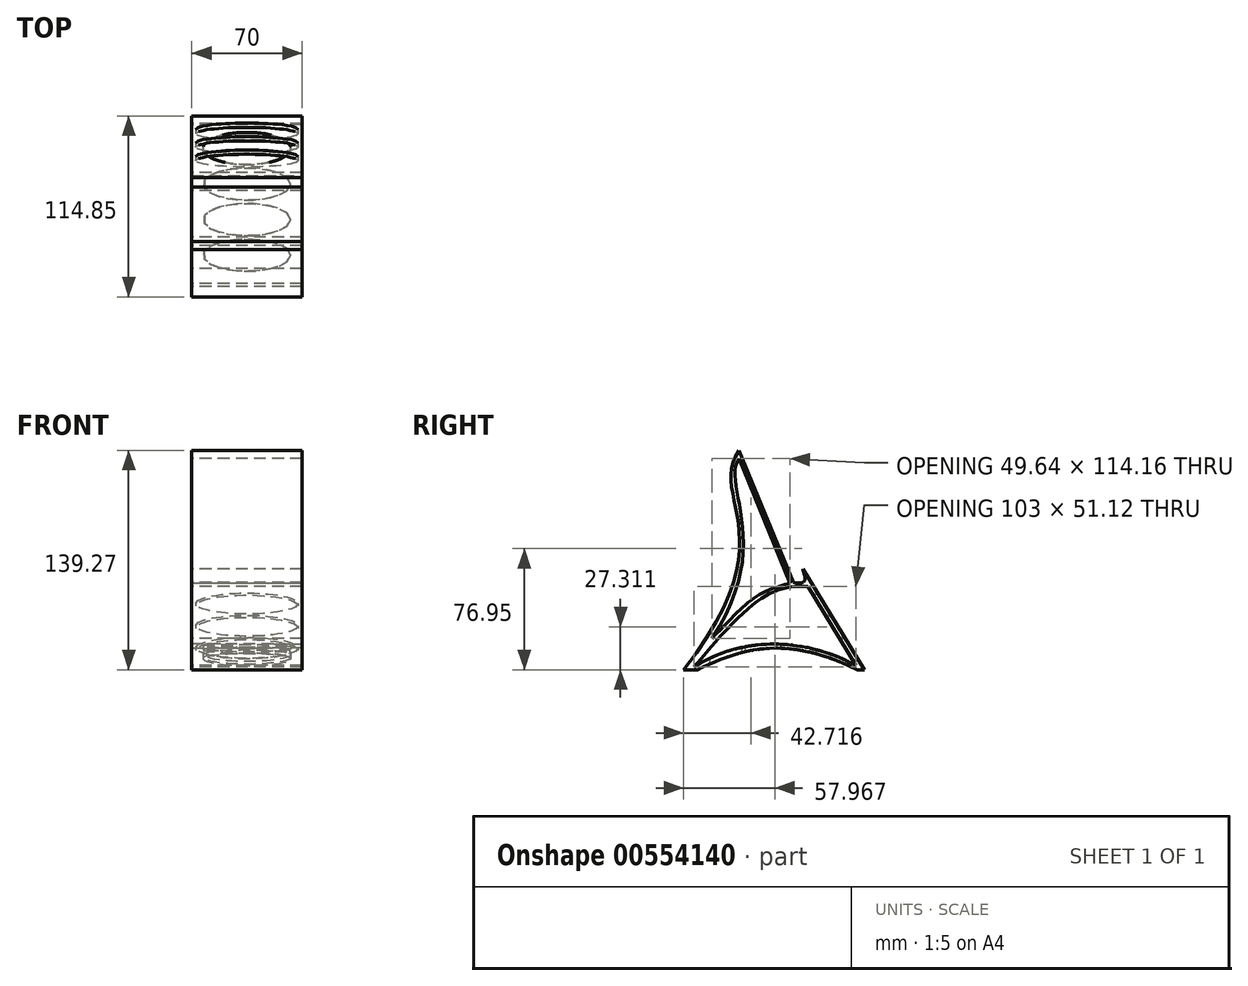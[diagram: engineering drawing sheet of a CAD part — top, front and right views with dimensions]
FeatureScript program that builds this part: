
annotation { "Feature Type Name" : "Feature", "Feature Type Description" : "" }
export const myFeature = defineFeature(function(context is Context, id is Id, definition is map)
    precondition{}
    {
        {
            var Q0;
            Q0=qCreatedBy(makeId("Right.planeOp"),FACE);
            var sketch = newSketch(context, id + "F0", { "sketchPlane" : qUnion([Q0])});
            skFitSpline(sketch, "E0", {"points": [v(-65.05, 0) * mm, v(-29.92, 139.27) * mm], "startDerivative": vector(201.71, 254.1) * mm, "endDerivative": vector(62.07, 87.75) * mm});
            skFitSpline(sketch, "E1", {"points": [v(-56.41, 0) * mm, v(45.2, 0) * mm], "startDerivative": vector(85.43, 39.38) * mm, "endDerivative": vector(140.76, -68.45) * mm});
            skFitSpline(sketch, "E2", {"points": [v(49.8, 0) * mm, v(10.74, 63.83) * mm], "startDerivative": vector(-39.06, 63.83) * mm, "endDerivative": vector(-39.06, 63.83) * mm});
            skLineSegment(sketch, "E3", {"start": v(-29.92, 139.27) * mm, "end": v(4.83, 55.39) * mm});
            skFitSpline(sketch, "E4", {"points": [v(-47.16, 19.87) * mm, v(4.83, 55.39) * mm], "startDerivative": vector(67.93, 68.5) * mm, "endDerivative": vector(79.95, 18.57) * mm});
            skFitSpline(sketch, "E5", {"points": [v(-47.16, 19.87) * mm, v(-29.9, 134.03) * mm], "startDerivative": vector(120.76, 180.8) * mm, "endDerivative": vector(35.66, 50.36) * mm});
            skFitSpline(sketch, "E6", {"points": [v(-58.58, 1.75) * mm, v(13.98, 52.87) * mm], "startDerivative": vector(111.53, 132.38) * mm, "endDerivative": vector(70.15, -3.04) * mm});
            skFitSpline(sketch, "E7", {"points": [v(-58.58, 1.75) * mm, v(44.42, 2.6) * mm], "startDerivative": vector(96.07, 60.59) * mm, "endDerivative": vector(95.42, -52.13) * mm});
            skFitSpline(sketch, "E8", {"points": [v(4.83, 55.39) * mm, v(10.74, 63.83) * mm], "startDerivative": vector(36.77, -7.47) * mm, "endDerivative": vector(2.44, 4) * mm});
            skLineSegment(sketch, "E9", {"start": v(-65.05, 0) * mm, "end": v(-56.41, 0) * mm});
            skLineSegment(sketch, "E10", {"start": v(45.2, 0) * mm, "end": v(49.8, 0) * mm});
            skLineSegment(sketch, "E11", {"start": v(13.98, 52.87) * mm, "end": v(44.42, 2.6) * mm});
            skLineSegment(sketch, "E12", {"start": v(-29.9, 134.03) * mm, "end": v(2.49, 54.83) * mm});
            skSolve(sketch);
        }
        {
            var Q0;
            Q0=makeQuery(id+"F0.imprint","IMPRINT",FACE,{"disambiguationData":[TD([[makeQuery(id+"F0.imprint","IMPRINT",EDGE,{"derivedFrom":sQuery(id+"F0.wireOp",EDGE,"E0")}),-1.0]])]});
            extrude(context, id + "F1", {"entities" : qUnion([Q0]), "depth" : 70 * mm});
        }
        {
            var Q0;
            Q0=makeQuery(id+"F1.opExtrude","SWEPT_FACE",FACE,{"disambiguationData":[OSD([sQuery(id+"F0.wireOp",EDGE,"3ry2OGPV-gmds-sl4L-2rMf-ZdiDfTWU18HU")])]});
            var Q1;
            Q1=makeQuery(id+"F1.opExtrude","SWEPT_EDGE",EDGE,{"disambiguationData":[OSD([sQuery(id+"F0.wireOp",EDGE,"E0"),sQuery(id+"F0.wireOp",EDGE,"E3")])]});
            cPlane(context, id + "F2", {"entities" : qUnion([Q0, Q1]), "cplaneType" : CPlaneType.LINE_ANGLE, "offset" : 25 * mm, "angle" : 90 * degree, "width" : 150 * mm, "height" : 150 * mm});
        }
        {
            var Q0;
            Q0=qCreatedBy(id+"F2.planeOp",FACE);
            var sketch = newSketch(context, id + "F3", { "sketchPlane" : qUnion([Q0])});
            skLineSegment(sketch, "E13.bottom", {"start": v(0, -20) * mm, "end": v(70, -20) * mm});
            skLineSegment(sketch, "E13.top", {"start": v(0, 53.36) * mm, "end": v(70, 53.36) * mm});
            skLineSegment(sketch, "E13.left", {"start": v(0, -20) * mm, "end": v(0, 53.36) * mm});
            skLineSegment(sketch, "E13.right", {"start": v(70, -20) * mm, "end": v(70, 53.36) * mm});
            skSolve(sketch);
        }
        {
            var Q0;
            Q0=qCreatedBy(id+"F2.planeOp",FACE);
            var sketch = newSketch(context, id + "F4", { "sketchPlane" : qUnion([Q0])});
            skEllipse(sketch, "E14", {"center": v(35, -10.4) * mm, "majorRadius": 32.5 * mm, "minorRadius": 8.5 * mm, "majorAxis": v(-1, 0)});
            skEllipse(sketch, "E15.0.1.0", {"center": v(35, 7.6) * mm, "majorRadius": 32.5 * mm, "minorRadius": 8.5 * mm, "majorAxis": v(-1, 0)});
            skEllipse(sketch, "E15.0.2.0", {"center": v(35, 25.6) * mm, "majorRadius": 32.5 * mm, "minorRadius": 8.5 * mm, "majorAxis": v(-1, 0)});
            skEllipse(sketch, "E15.0.3.0", {"center": v(35, 43.6) * mm, "majorRadius": 32.5 * mm, "minorRadius": 8.5 * mm, "majorAxis": v(-1, 0)});
            skLineSegment(sketch, "E15.direction1", {"start": v(35, -10.4) * mm, "end": v(60, -10.4) * mm, "construction": true});
            skLineSegment(sketch, "E15.direction2", {"start": v(35, -10.4) * mm, "end": v(35, 7.6) * mm, "construction": true});
            skSolve(sketch);
        }
        {
            var Q0;
            Q0=qSketchRegion(id+"F4",true);
            extrude(context, id + "F5", {"entities" : qUnion([Q0]), "operationType" : NewBodyOperationType.REMOVE, "endBound" : BoundingType.THROUGH_ALL, "depth" : 25 * mm});
        }
        {
            var Q0;
            Q0=qCreatedBy(id+"F2.planeOp",FACE);
            var sketch = newSketch(context, id + "F6", { "sketchPlane" : qUnion([Q0])});
            skEllipse(sketch, "E16", {"center": v(35.28, -29.36) * mm, "majorRadius": 17.78 * mm, "minorRadius": 3.94 * mm, "majorAxis": v(-1, 0)});
            skSolve(sketch);
        }
        {
            var Q0;
            Q0=qSketchRegion(id+"F6",true);
            extrude(context, id + "F7", {"entities" : qUnion([Q0]), "operationType" : NewBodyOperationType.REMOVE, "endBound" : BoundingType.THROUGH_ALL, "depth" : 25 * mm});
        }
        {
            var Q0;
            Q0=makeQuery(id+"F1.opExtrude","SWEPT_FACE",FACE,{"disambiguationData":[OSD([sQuery(id+"F0.wireOp",EDGE,"E11")])]});
            var sketch = newSketch(context, id + "F8", { "sketchPlane" : qUnion([Q0])});
            skEllipse(sketch, "E17", {"center": v(35, 23.43) * mm, "majorRadius": 32.5 * mm, "minorRadius": 7.82 * mm, "majorAxis": v(1, 0)});
            skEllipse(sketch, "E18.0.1.0", {"center": v(35, 6.93) * mm, "majorRadius": 32.5 * mm, "minorRadius": 7.82 * mm, "majorAxis": v(1, 0)});
            skEllipse(sketch, "E18.0.2.0", {"center": v(35, -9.57) * mm, "majorRadius": 32.5 * mm, "minorRadius": 7.82 * mm, "majorAxis": v(1, 0)});
            skLineSegment(sketch, "E18.direction1", {"start": v(35, 23.43) * mm, "end": v(57.03, 23.43) * mm, "construction": true});
            skLineSegment(sketch, "E18.direction2", {"start": v(35, 23.43) * mm, "end": v(35, 6.93) * mm, "construction": true});
            skSolve(sketch);
        }
        {
            var Q0;
            Q0=qSketchRegion(id+"F8",true);
            var Q1;
            Q1=makeQuery(id+"F1.opExtrude","SWEPT_FACE",FACE,{"disambiguationData":[OSD([sQuery(id+"F0.wireOp",EDGE,"E2")])]});
            extrude(context, id + "F9", {"entities" : qUnion([Q0]), "operationType" : NewBodyOperationType.REMOVE, "endBound" : BoundingType.UP_TO_SURFACE, "oppositeDirection" : true, "endBoundEntityFace" : qUnion([Q1]), "depth" : 25 * mm});
        }
        {
            var Q0;
            Q0=qCreatedBy(makeId("Top.planeOp"),FACE);
            var sketch = newSketch(context, id + "F10", { "sketchPlane" : qUnion([Q0])});
            skEllipse(sketch, "E19", {"center": v(35, -38.54) * mm, "majorRadius": 27.85 * mm, "minorRadius": 10.2 * mm, "majorAxis": v(1, 0)});
            skEllipse(sketch, "E20.0.1.0", {"center": v(35, -15.94) * mm, "majorRadius": 27.85 * mm, "minorRadius": 10.2 * mm, "majorAxis": v(1, 0)});
            skEllipse(sketch, "E20.0.2.0", {"center": v(35, 6.66) * mm, "majorRadius": 27.85 * mm, "minorRadius": 10.2 * mm, "majorAxis": v(1, 0)});
            skEllipse(sketch, "E20.0.3.0", {"center": v(35, 29.26) * mm, "majorRadius": 27.85 * mm, "minorRadius": 10.2 * mm, "majorAxis": v(1, 0)});
            skLineSegment(sketch, "E20.direction1", {"start": v(35, -38.54) * mm, "end": v(60, -38.54) * mm, "construction": true});
            skLineSegment(sketch, "E20.direction2", {"start": v(35, -38.54) * mm, "end": v(35, -15.94) * mm, "construction": true});
            skSolve(sketch);
        }
        {
            var Q0;
            Q0=qSketchRegion(id+"F10",true);
            var Q1;
            Q1=makeQuery(id+"F1.opExtrude","SWEPT_FACE",FACE,{"disambiguationData":[OSD([sQuery(id+"F0.wireOp",EDGE,"E7")])]});
            extrude(context, id + "F11", {"entities" : qUnion([Q0]), "operationType" : NewBodyOperationType.REMOVE, "endBound" : BoundingType.UP_TO_SURFACE, "endBoundEntityFace" : qUnion([Q1]), "depth" : 25 * mm});
        }
    });
